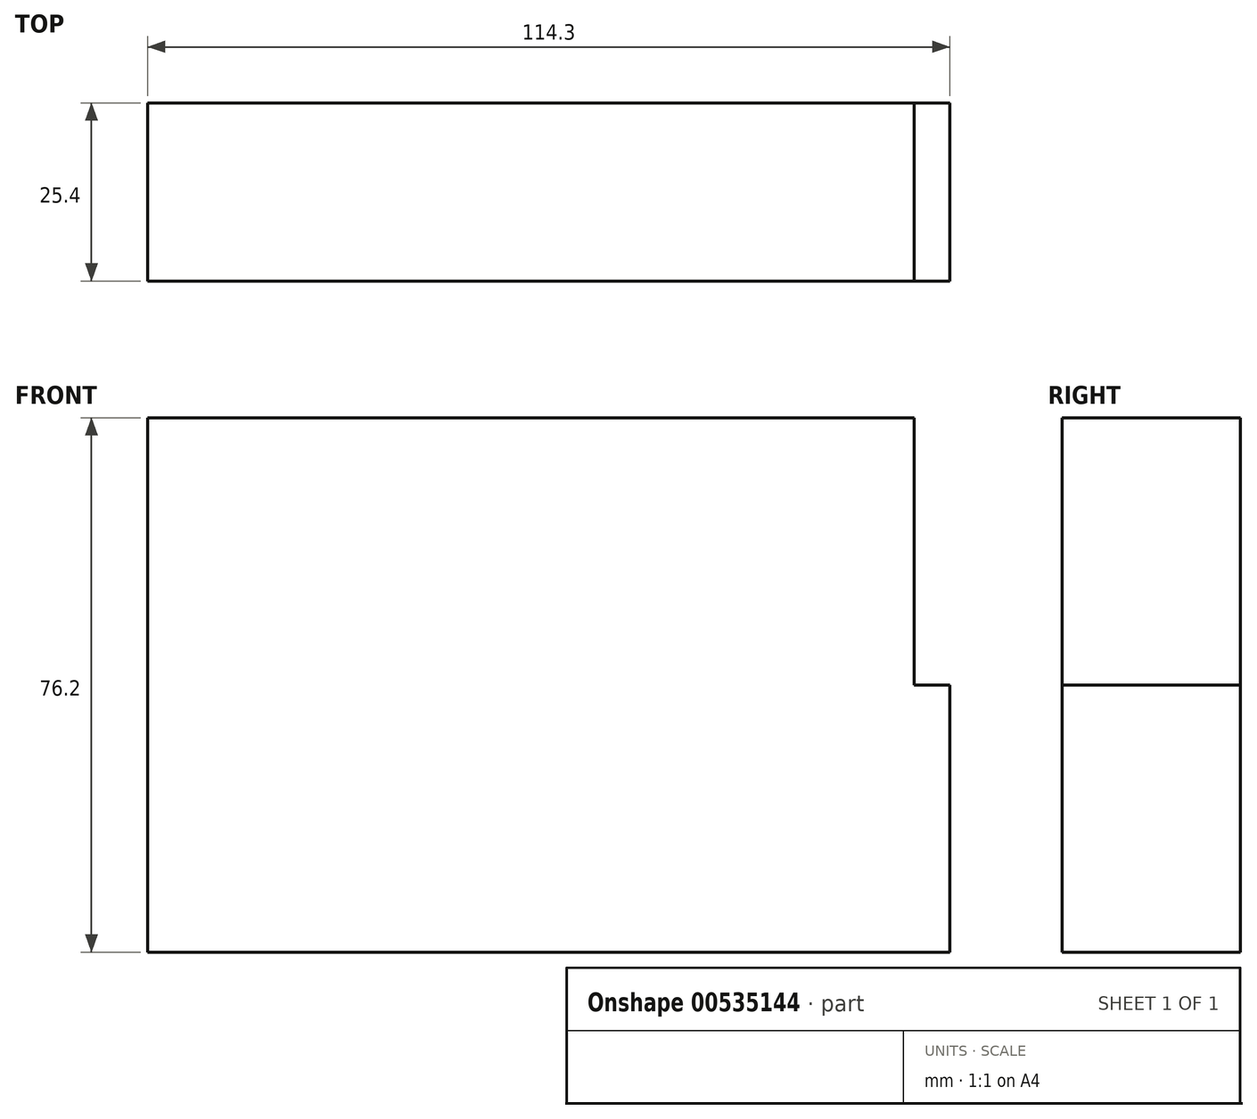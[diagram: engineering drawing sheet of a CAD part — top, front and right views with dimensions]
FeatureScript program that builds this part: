
annotation { "Feature Type Name" : "Feature", "Feature Type Description" : "" }
export const myFeature = defineFeature(function(context is Context, id is Id, definition is map)
    precondition{}
    {
        {
            var Q0;
            Q0=qCreatedBy(makeId("Front.planeOp"),FACE);
            var sketch = newSketch(context, id + "F0", { "sketchPlane" : qUnion([Q0])});
            skLineSegment(sketch, "E0.bottom", {"start": v(0, 0) * mm, "end": v(114.3, 0) * mm});
            skLineSegment(sketch, "E0.top", {"start": v(0, 76.2) * mm, "end": v(109.22, 76.2) * mm});
            skLineSegment(sketch, "E0.left", {"start": v(0, 0) * mm, "end": v(0, 76.2) * mm});
            skLineSegment(sketch, "E0.right", {"start": v(114.3, 0) * mm, "end": v(114.3, 38.1) * mm});
            skLineSegment(sketch, "E1.top", {"start": v(114.3, 38.1) * mm, "end": v(109.22, 38.1) * mm});
            skLineSegment(sketch, "E1.right", {"start": v(109.22, 76.2) * mm, "end": v(109.22, 38.1) * mm});
            skSolve(sketch);
        }
        {
            var Q0;
            Q0=qSketchRegion(id+"F0",true);
            extrude(context, id + "F1", {"entities" : qUnion([Q0]), "depth" : 25.4 * mm});
        }
    });
